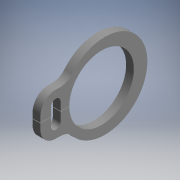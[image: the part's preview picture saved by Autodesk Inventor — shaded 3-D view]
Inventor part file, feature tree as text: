
AUTODESK INVENTOR PART (.ipt)
format: ipt  version: 2017.3 (Build 213256000, 256)  size: 125,440 bytes
history: native  units: mm (DEFAULTED — no unit token found)
features: other x14, extrude x1, sketch x1
ambient origin geometry x8: Origin, YZ Plane, XZ Plane, XY Plane, X Axis, Y Axis, Z Axis, Center Point
bodies: Solid1 (feature_tree)
feature tree (16):
  extrude  "Extrusion1"  TaperAngle=0.0deg  [1 undecoded]
  other  "1_XY"
  other  "1_YZ"
  other  "1_ZX"
  other  "1_X"
  other  "1_Y"
  other  "1_Z"
  other  "1_Center"
  other  "combination_module_XY"
  other  "combination_module_YZ"
  other  "combination_module_ZX"
  other  "combination_module_X"
  other  "combination_module_Y"
  other  "combination_module_Z"
  other  "combination_module_Center"
  sketch  "Sketch_5"  dims[d0=0.8mm d1=0.0mm d2=0.0mm]
note: 1 required parameter value undecoded (feature->parameter linkage not recoverable at this tier; creation-order binding heuristic only, values carry confidence <= 0.55)
